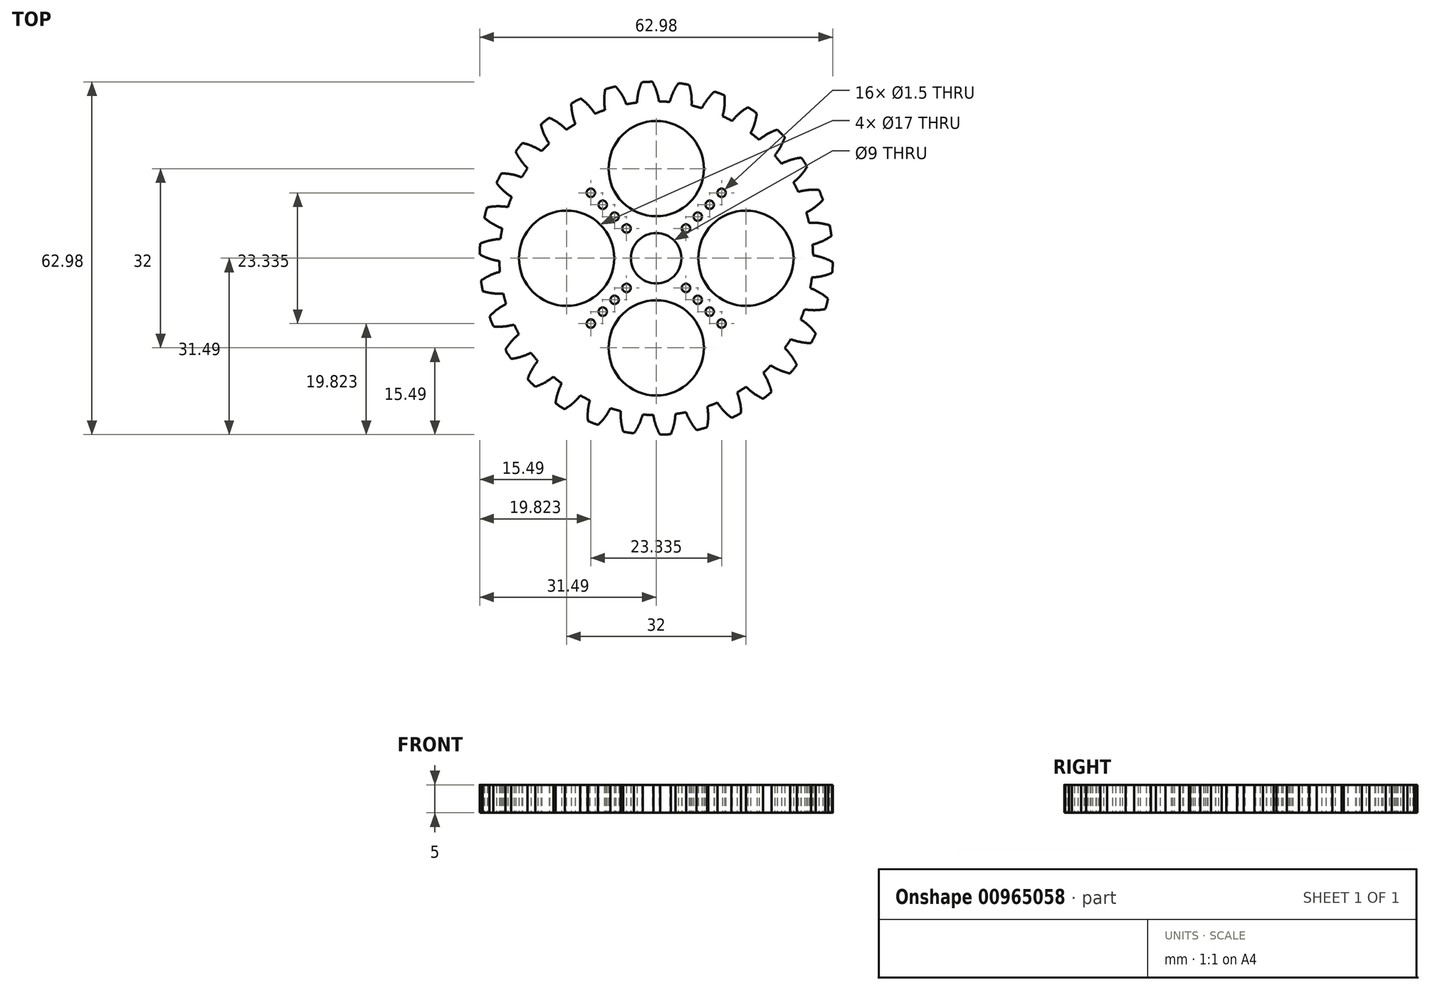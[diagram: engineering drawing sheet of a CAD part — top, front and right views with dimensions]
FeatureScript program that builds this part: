
annotation { "Feature Type Name" : "Feature", "Feature Type Description" : "" }
export const myFeature = defineFeature(function(context is Context, id is Id, definition is map)
    precondition{}
    {
        {
            var Q0;
            Q0=qCreatedBy(makeId("Top.planeOp"),FACE);
            var sketch = newSketch(context, id + "F0", { "sketchPlane" : qUnion([Q0])});
            skCircle(sketch, "E0", {"center": v(0, 0) * mm, "radius": 31.5 * mm, "construction": true});
            skCircle(sketch, "E1", {"center": v(0, 0) * mm, "radius": 30 * mm, "construction": true});
            skCircle(sketch, "E2", {"center": v(0, 0) * mm, "radius": 28 * mm});
            skLineSegment(sketch, "E3", {"start": v(0, 0) * mm, "end": v(0, 40.6) * mm, "construction": true});
            skLineSegment(sketch, "E4", {"start": v(0, 0) * mm, "end": v(-2.13, 40.73) * mm, "construction": true});
            skLineSegment(sketch, "E5", {"start": v(0, 30) * mm, "end": v(-44.2, 30) * mm, "construction": true});
            skLineSegment(sketch, "E6", {"start": v(0, 30) * mm, "end": v(-43.84, 14.04) * mm, "construction": true});
            skLineSegment(sketch, "E7", {"start": v(0, 0) * mm, "end": v(-9.64, 26.5) * mm, "construction": true});
            skCircle(sketch, "E8", {"center": v(0, 0) * mm, "radius": 28.2 * mm, "construction": true});
            skCircle(sketch, "E9", {"center": v(0, 30) * mm, "radius": 10.26 * mm, "construction": true});
            skCircle(sketch, "E10", {"center": v(-9.64, 26.5) * mm, "radius": 10.26 * mm, "construction": true});
            skCircle(sketch, "E11", {"center": v(0, 0) * mm, "radius": 4.5 * mm});
            skCircle(sketch, "E12", {"center": v(16, 0) * mm, "radius": 8.5 * mm});
            skCircle(sketch, "E13", {"center": v(0, -16) * mm, "radius": 8.5 * mm});
            skCircle(sketch, "E14", {"center": v(-16, 0) * mm, "radius": 8.5 * mm});
            skCircle(sketch, "E15", {"center": v(0, 16) * mm, "radius": 8.5 * mm});
            skArc(sketch, "E16", {"start": v(0, 30) * mm, "mid": v(-0.31, 30.76) * mm, "end": v(-0.68, 31.5) * mm});
            skArc(sketch, "E17", {"start": v(0.5, 28) * mm, "mid": v(0.3, 29.01) * mm, "end": v(0, 30) * mm});
            skArc(sketch, "E18.MirrorCS", {"start": v(-3.14, 29.84) * mm, "mid": v(-2.9, 30.62) * mm, "end": v(-2.61, 31.4) * mm});
            skArc(sketch, "E19.MirrorCS", {"start": v(-3.43, 27.79) * mm, "mid": v(-3.33, 28.82) * mm, "end": v(-3.14, 29.84) * mm});
            skArc(sketch, "E20", {"start": v(-0.68, 31.5) * mm, "mid": v(-1.65, 31.47) * mm, "end": v(-2.61, 31.4) * mm});
            skLineSegment(sketch, "E21", {"start": v(0, 0) * mm, "end": v(37.1, 37.1) * mm, "construction": true});
            skLineSegment(sketch, "E22", {"start": v(0, 0) * mm, "end": v(-35.66, -35.66) * mm, "construction": true});
            skLineSegment(sketch, "E23", {"start": v(0, 0) * mm, "end": v(33.95, -33.95) * mm, "construction": true});
            skLineSegment(sketch, "E24", {"start": v(0, 0) * mm, "end": v(-39.23, 39.23) * mm, "construction": true});
            skCircle(sketch, "E25", {"center": v(5.3, 5.3) * mm, "radius": 0.75 * mm});
            skCircle(sketch, "E26", {"center": v(7.42, 7.42) * mm, "radius": 0.75 * mm});
            skCircle(sketch, "E27", {"center": v(9.55, 9.55) * mm, "radius": 0.75 * mm});
            skCircle(sketch, "E28", {"center": v(11.67, 11.67) * mm, "radius": 0.75 * mm});
            skCircle(sketch, "E29", {"center": v(-5.3, -5.3) * mm, "radius": 0.75 * mm});
            skCircle(sketch, "E30", {"center": v(-7.42, -7.42) * mm, "radius": 0.75 * mm});
            skCircle(sketch, "E31", {"center": v(-9.55, -9.55) * mm, "radius": 0.75 * mm});
            skCircle(sketch, "E32", {"center": v(-11.67, -11.67) * mm, "radius": 0.75 * mm});
            skCircle(sketch, "E33", {"center": v(5.3, -5.3) * mm, "radius": 0.75 * mm});
            skCircle(sketch, "E34", {"center": v(7.42, -7.42) * mm, "radius": 0.75 * mm});
            skCircle(sketch, "E35", {"center": v(9.55, -9.55) * mm, "radius": 0.75 * mm});
            skCircle(sketch, "E36", {"center": v(11.67, -11.67) * mm, "radius": 0.75 * mm});
            skCircle(sketch, "E37", {"center": v(-5.3, 5.3) * mm, "radius": 0.75 * mm});
            skCircle(sketch, "E38", {"center": v(-7.42, 7.42) * mm, "radius": 0.75 * mm});
            skCircle(sketch, "E39", {"center": v(-9.55, 9.55) * mm, "radius": 0.75 * mm});
            skCircle(sketch, "E40", {"center": v(-11.67, 11.67) * mm, "radius": 0.75 * mm});
            skSolve(sketch);
        }
        {
            var Q0;
            {var subQ0=sQuery(id+"F0.wireOp",EDGE,"E2");var subQ1=makeQuery(id+"F0.imprint","INTERSECT",VERTEX,{"derivedFrom":[subQ0,sQuery(id+"F0.wireOp",EDGE,"H4GpqcEF-i2jk-b9H1-gogr-vYiBd7hIRJoO")]});Q0=makeQuery(id+"F0.imprint","IMPRINT",FACE,{"disambiguationData":[TD([[makeQuery(id+"F0.imprint","IMPRINT",EDGE,{"disambiguationData":[TD([[subQ1,-1.0]])],"derivedFrom":subQ0}),1.0]])]});}
            var Q1;
            Q1=makeQuery(id+"F0.imprint","IMPRINT",FACE,{"disambiguationData":[TD([[makeQuery(id+"F0.imprint","IMPRINT",EDGE,{"derivedFrom":sQuery(id+"F0.wireOp",EDGE,"Viipwr1V-t2mu-DFZV-wVTb-g0TGzVeT3VFk")}),1.0]])]});
            var Q2;
            Q2=makeQuery(id+"F0.imprint","IMPRINT",FACE,{"disambiguationData":[TD([[makeQuery(id+"F0.imprint","IMPRINT",EDGE,{"derivedFrom":sQuery(id+"F0.wireOp",EDGE,"E16")}),1.0]])]});
            extrude(context, id + "F1", {"entities" : qUnion([Q0, Q1, Q2]), "depth" : 5 * mm, "offsetDistance" : 25 * mm});
        }
        {
            var Q0;
            Q0=makeQuery(id+"F1.opExtrude","SWEPT_FACE",FACE,{"disambiguationData":[OSD([sQuery(id+"F0.wireOp",EDGE,"E16")])]});
            var Q1;
            Q1=makeQuery(id+"F1.opExtrude","SWEPT_FACE",FACE,{"disambiguationData":[OSD([sQuery(id+"F0.wireOp",EDGE,"E17")])]});
            var Q2;
            Q2=makeQuery(id+"F1.opExtrude","SWEPT_FACE",FACE,{"disambiguationData":[OSD([sQuery(id+"F0.wireOp",EDGE,"E20")])]});
            var Q3;
            Q3=makeQuery(id+"F1.opExtrude","SWEPT_FACE",FACE,{"disambiguationData":[OSD([sQuery(id+"F0.wireOp",EDGE,"E18.MirrorCS")])]});
            var Q4;
            Q4=makeQuery(id+"F1.opExtrude","SWEPT_FACE",FACE,{"disambiguationData":[OSD([sQuery(id+"F0.wireOp",EDGE,"E19.MirrorCS")])]});
            var Q5;
            Q5=makeQuery(id+"F1.opExtrude","SWEPT_FACE",FACE,{"disambiguationData":[OSD([sQuery(id+"F0.wireOp",EDGE,"E2")])]});
            circularPattern(context, id + "F2", {"patternType" : PatternType.FACE, "faces" : qUnion([Q0, Q1, Q2, Q3, Q4]), "axis" : qUnion([Q5]), "angle" : 360 * degree, "instanceCount" : 30, "equalSpace" : true});
        }
    });
